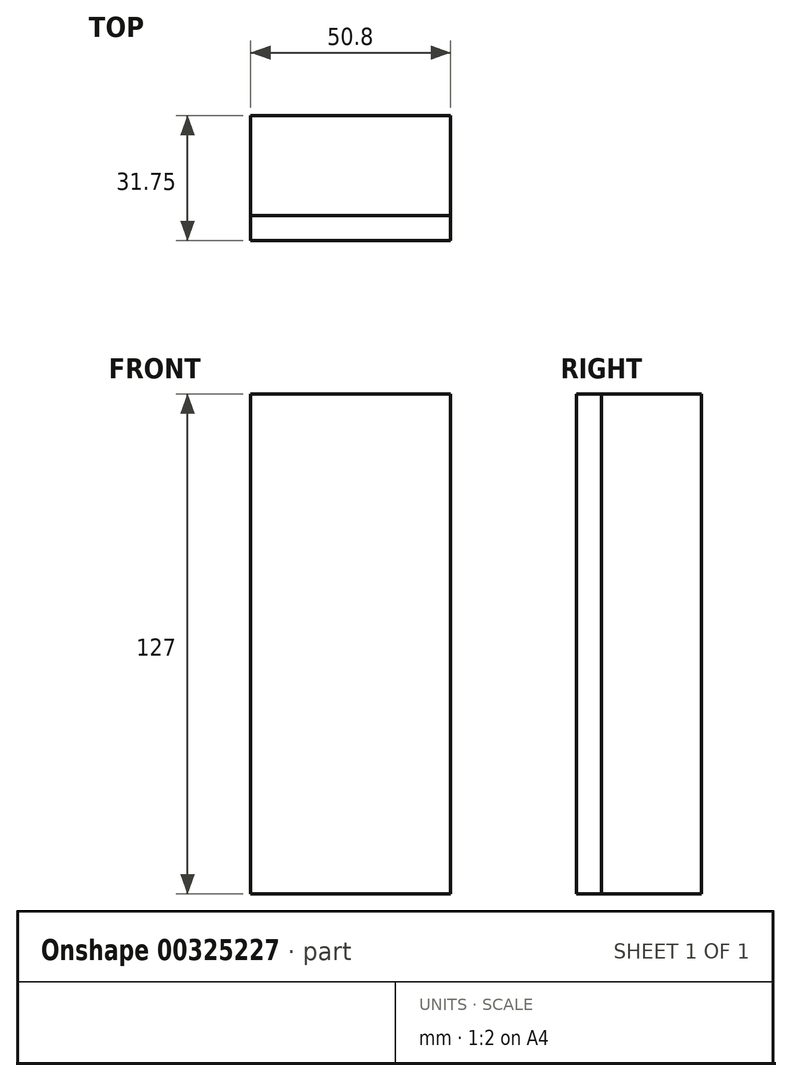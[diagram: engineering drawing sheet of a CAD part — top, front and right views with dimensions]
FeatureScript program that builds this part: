
annotation { "Feature Type Name" : "Feature", "Feature Type Description" : "" }
export const myFeature = defineFeature(function(context is Context, id is Id, definition is map)
    precondition{}
    {
        {
            var Q0;
            Q0=qCreatedBy(makeId("Top.planeOp"),FACE);
            var sketch = newSketch(context, id + "F0", { "sketchPlane" : qUnion([Q0])});
            skLineSegment(sketch, "E0.bottom", {"start": v(0, 0) * mm, "end": v(50.8, 0) * mm});
            skLineSegment(sketch, "E0.top", {"start": v(0, 25.4) * mm, "end": v(50.8, 25.4) * mm});
            skLineSegment(sketch, "E0.left", {"start": v(0, 0) * mm, "end": v(0, 25.4) * mm});
            skLineSegment(sketch, "E0.right", {"start": v(50.8, 0) * mm, "end": v(50.8, 25.4) * mm});
            skSolve(sketch);
        }
        {
            var Q0;
            Q0=makeQuery(id+"F0.imprint","IMPRINT",FACE,{"disambiguationData":[TD([[makeQuery(id+"F0.imprint","IMPRINT",EDGE,{"derivedFrom":sQuery(id+"F0.wireOp",EDGE,"E0.bottom")}),1.0]])]});
            extrude(context, id + "F1", {"entities" : qUnion([Q0]), "depth" : 127 * mm});
        }
        {
            var Q0;
            Q0=makeQuery(id+"F1.opExtrude","SWEPT_FACE",FACE,{"disambiguationData":[OSD([sQuery(id+"F0.wireOp",EDGE,"E0.bottom")])]});
            extrude(context, id + "F2", {"entities" : qUnion([Q0]), "depth" : 6.35 * mm});
        }
    });
